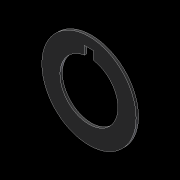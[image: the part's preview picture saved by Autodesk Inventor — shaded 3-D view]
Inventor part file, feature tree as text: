
AUTODESK INVENTOR PART (.ipt)
format: ipt  version: unknown  size: 164,352 bytes
history: native  units: in
note: dims shown in document units (in); Inventor stores cm internally (conversion verified against a paired STEP export)
features: extrude x1, sketch x1, reference x1
ambient origin geometry x8: Origin, YZ Plane, XZ Plane, XY Plane, X Axis, Y Axis, Z Axis, Center Point
feature tree (3):
  extrude  "Extrusion1"  Depth=1.429in
  sketch  "Sketch1"  dims[d0=0.037in d1=0.0in d2=1.429in]
  reference  "Reference1"
